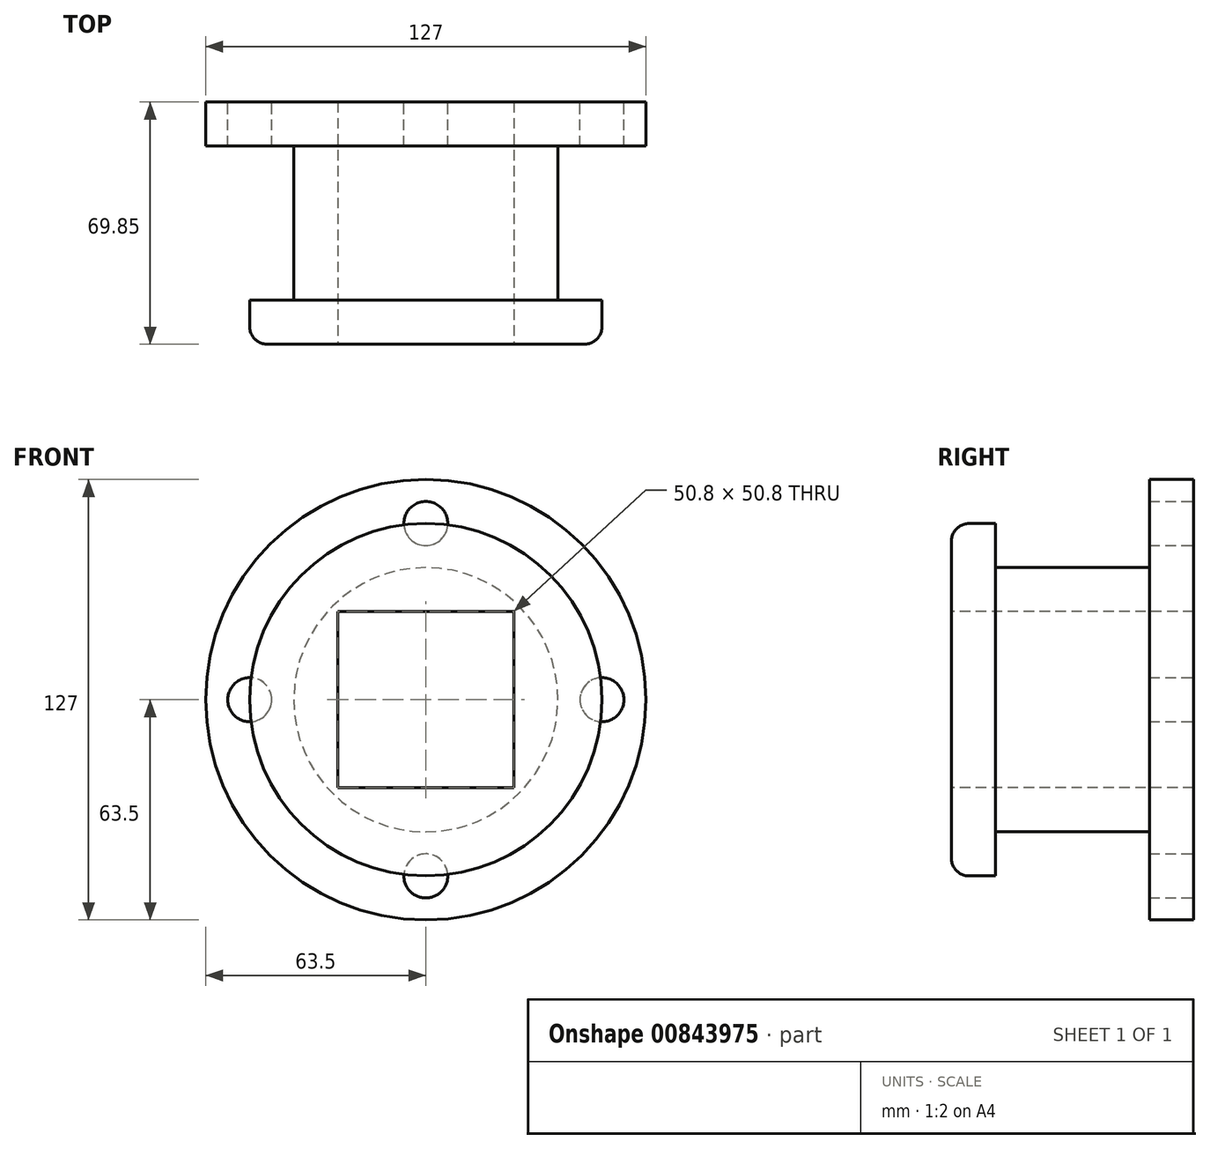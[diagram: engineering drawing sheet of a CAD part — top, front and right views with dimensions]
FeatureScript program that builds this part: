
annotation { "Feature Type Name" : "Feature", "Feature Type Description" : "" }
export const myFeature = defineFeature(function(context is Context, id is Id, definition is map)
    precondition{}
    {
        {
            var Q0;
            Q0=qCreatedBy(makeId("Front.planeOp"),FACE);
            var sketch = newSketch(context, id + "F0", { "sketchPlane" : qUnion([Q0])});
            skCircle(sketch, "E0", {"center": v(0, 0) * mm, "radius": 63.5 * mm});
            skSolve(sketch);
        }
        {
            var Q0;
            Q0 = qSketchRegion(id + "F0", true);
            extrude(context, id + "F1", {"entities" : qUnion([Q0]), "depth" : 12.7 * mm, "offsetDistance" : 25.4 * mm});
        }
        {
            var Q0;
            Q0=qCreatedBy(makeId("Front.planeOp"),FACE);
            var sketch = newSketch(context, id + "F2", { "sketchPlane" : qUnion([Q0])});
            skCircle(sketch, "E1", {"center": v(0, 50.8) * mm, "radius": 6.35 * mm});
            skCircle(sketch, "E2.1.0", {"center": v(-50.8, 0) * mm, "radius": 6.35 * mm});
            skCircle(sketch, "E2.2.0", {"center": v(0, -50.8) * mm, "radius": 6.35 * mm});
            skCircle(sketch, "E2.3.0", {"center": v(50.8, 0) * mm, "radius": 6.35 * mm});
            skPoint(sketch, "E2.center", {"position": v(0, 0) * mm});
            skSolve(sketch);
        }
        {
            var Q0;
            Q0 = qSketchRegion(id + "F2", true);
            extrude(context, id + "F3", {"entities" : qUnion([Q0]), "operationType" : NewBodyOperationType.REMOVE, "depth" : 12.7 * mm, "offsetDistance" : 25.4 * mm});
        }
        {
            var Q0;
            Q0=qCreatedBy(makeId("Front.planeOp"),FACE);
            var sketch = newSketch(context, id + "F4", { "sketchPlane" : qUnion([Q0])});
            skCircle(sketch, "E3", {"center": v(0, 0) * mm, "radius": 38.1 * mm});
            skSolve(sketch);
        }
        {
            var Q0;
            Q0 = qSketchRegion(id + "F4", true);
            extrude(context, id + "F5", {"entities" : qUnion([Q0]), "operationType" : NewBodyOperationType.ADD, "depth" : 57.15 * mm, "offsetDistance" : 25.4 * mm});
        }
        {
            var Q0;
            Q0=makeQuery(id+"F5.opExtrude","CAP_FACE",FACE,{"disambiguationData":[OSD([sQuery(id+"F4.wireOp",EDGE,"E3")])],"isStart":false});
            var sketch = newSketch(context, id + "F6", { "sketchPlane" : qUnion([Q0])});
            skCircle(sketch, "E4", {"center": v(0, 0) * mm, "radius": 50.8 * mm});
            skSolve(sketch);
        }
        {
            var Q0;
            Q0 = qSketchRegion(id + "F6", true);
            extrude(context, id + "F7", {"entities" : qUnion([Q0]), "operationType" : NewBodyOperationType.ADD, "depth" : 12.7 * mm, "offsetDistance" : 25.4 * mm});
        }
        {
            var Q0;
            Q0=makeQuery(id+"F7.opExtrude","CAP_FACE",FACE,{"disambiguationData":[OSD([sQuery(id+"F6.wireOp",EDGE,"E4")])],"isStart":false});
            var sketch = newSketch(context, id + "F8", { "sketchPlane" : qUnion([Q0])});
            skLineSegment(sketch, "E5.bottom", {"start": v(25.4, 25.4) * mm, "end": v(-25.4, 25.4) * mm});
            skLineSegment(sketch, "E5.top", {"start": v(25.4, -25.4) * mm, "end": v(-25.4, -25.4) * mm});
            skLineSegment(sketch, "E5.left", {"start": v(25.4, 25.4) * mm, "end": v(25.4, -25.4) * mm});
            skLineSegment(sketch, "E5.right", {"start": v(-25.4, 25.4) * mm, "end": v(-25.4, -25.4) * mm});
            skPoint(sketch, "E5.middle", {"position": v(0, 0) * mm});
            skSolve(sketch);
        }
        {
            var Q0;
            Q0 = qSketchRegion(id + "F8", true);
            var Q1;
            Q1=makeQuery(id+"F8.imprint","IMPRINT",FACE,{"disambiguationData":[TD([[makeQuery(id+"F8.imprint","IMPRINT",EDGE,{"derivedFrom":sQuery(id+"F8.wireOp",EDGE,"E5.bottom")}),1.0]])]});
            extrude(context, id + "F9", {"entities" : qUnion([Q0, Q1]), "operationType" : NewBodyOperationType.REMOVE, "oppositeDirection" : true, "depth" : 82.55 * mm, "offsetDistance" : 25.4 * mm});
        }
        {
            var Q0;
            Q0=makeQuery(id+"F7.opExtrude","CAP_EDGE",EDGE,{"disambiguationData":[OSD([sQuery(id+"F6.wireOp",EDGE,"E4")])],"isStart":false});
            fillet(context, id + "F10", {"entities" : qUnion([Q0]), "radius" : 5.08 * mm, "tangentPropagation" : true, "allowEdgeOverflow" : false});
        }
    });
